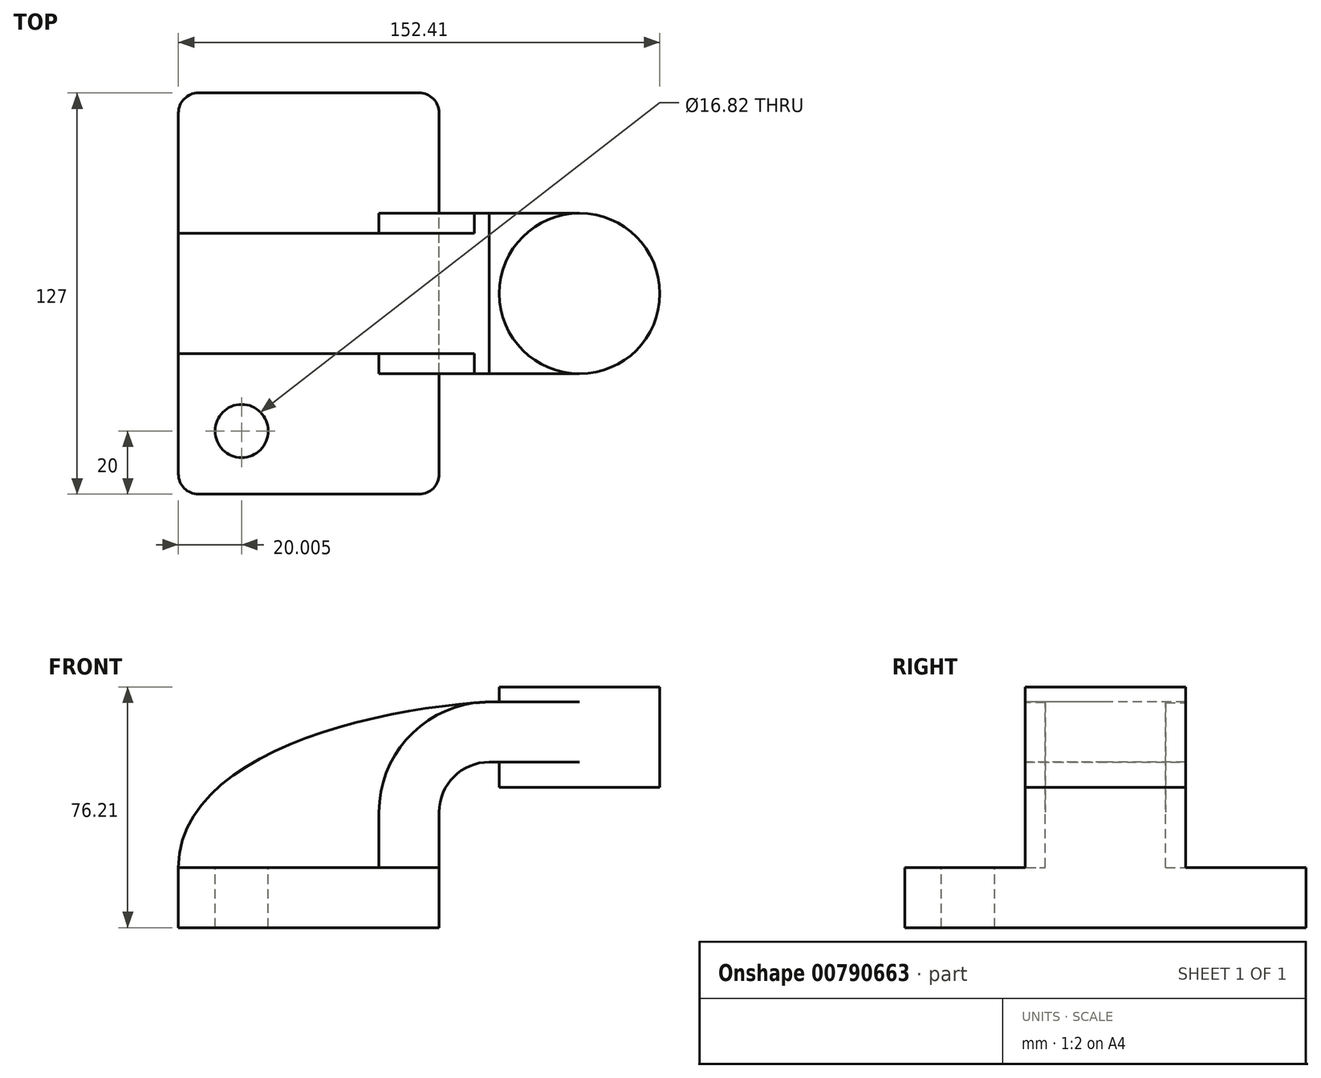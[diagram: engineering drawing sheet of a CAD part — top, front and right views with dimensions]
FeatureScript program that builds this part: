
annotation { "Feature Type Name" : "Feature", "Feature Type Description" : "" }
export const myFeature = defineFeature(function(context is Context, id is Id, definition is map)
    precondition{}
    {
        {
            var Q0;
            Q0=qCreatedBy(makeId("Front.planeOp"),FACE);
            var sketch = newSketch(context, id + "F0", { "sketchPlane" : qUnion([Q0])});
            skLineSegment(sketch, "E0.bottom", {"start": v(41.28, -9.52) * mm, "end": v(-41.28, -9.53) * mm});
            skLineSegment(sketch, "E0.top", {"start": v(41.28, 9.53) * mm, "end": v(-41.28, 9.53) * mm});
            skLineSegment(sketch, "E0.left", {"start": v(41.28, -9.52) * mm, "end": v(41.28, 9.53) * mm});
            skLineSegment(sketch, "E0.right", {"start": v(-41.28, -9.52) * mm, "end": v(-41.28, 9.53) * mm});
            skPoint(sketch, "E0.middle", {"position": v(0, 0) * mm});
            skLineSegment(sketch, "E1.bottom", {"start": v(111.12, 34.93) * mm, "end": v(60.32, 34.93) * mm});
            skLineSegment(sketch, "E1.top", {"start": v(111.12, 66.68) * mm, "end": v(60.32, 66.68) * mm});
            skLineSegment(sketch, "E1.left", {"start": v(111.12, 34.93) * mm, "end": v(111.12, 66.68) * mm});
            skLineSegment(sketch, "E1.right", {"start": v(60.32, 34.93) * mm, "end": v(60.32, 66.68) * mm});
            skPoint(sketch, "E1.middle", {"position": v(85.72, 50.8) * mm});
            skLineSegment(sketch, "E2", {"start": v(41.28, 9.53) * mm, "end": v(41.28, 27) * mm});
            skArc(sketch, "E3", {"start": v(41.27, 27) * mm, "mid": v(45.92, 38.23) * mm, "end": v(57.15, 42.88) * mm});
            skLineSegment(sketch, "E4", {"start": v(57.15, 42.88) * mm, "end": v(85.72, 42.88) * mm});
            skLineSegment(sketch, "E5.0", {"start": v(57.15, 61.93) * mm, "end": v(85.72, 61.93) * mm});
            skArc(sketch, "E5.1", {"start": v(22.23, 27) * mm, "mid": v(32.45, 51.7) * mm, "end": v(57.15, 61.93) * mm});
            skLineSegment(sketch, "E5.2", {"start": v(22.22, 9.53) * mm, "end": v(22.22, 27) * mm});
            skLineSegment(sketch, "E6", {"start": v(85.72, 34.93) * mm, "end": v(85.72, 66.68) * mm});
            skFitSpline(sketch, "E7", {"points": [v(-41.28, 9.52) * mm, v(57.15, 61.93) * mm], "startDerivative": vector(0.89, 108.07) * mm, "endDerivative": vector(112.76, 6.3) * mm});
            skSolve(sketch);
        }
        {
            var Q0;
            Q0=makeQuery(id+"F0.imprint","IMPRINT",FACE,{"disambiguationData":[TD([[makeQuery(id+"F0.imprint","IMPRINT",EDGE,{"derivedFrom":sQuery(id+"F0.wireOp",EDGE,"E0.bottom")}),-1.0]])]});
            extrude(context, id + "F1", {"entities" : qUnion([Q0]), "endBound" : BoundingType.SYMMETRIC, "depth" : 127 * mm, "offsetDistance" : 25.4 * mm});
        }
        {
            var Q0;
            {var subQ1=sQuery(id+"F0.wireOp",EDGE,"E2");Q0=makeQuery(id+"F0.imprint","IMPRINT",FACE,{"disambiguationData":[TD([[makeQuery(id+"F0.imprint","IMPRINT",EDGE,{"derivedFrom":subQ1}),1.0]])]});}
            var Q1;
            {var subQ0=sQuery(id+"F0.wireOp",EDGE,"E4");var subQ1=sQuery(id+"F0.wireOp",EDGE,"E1.right");var subQ2=makeQuery(id+"F0.imprint","INTERSECT",VERTEX,{"derivedFrom":[subQ1,subQ0]});Q1=makeQuery(id+"F0.imprint","IMPRINT",FACE,{"disambiguationData":[TD([[makeQuery(id+"F0.imprint","IMPRINT",EDGE,{"disambiguationData":[TD([[subQ2,-1.0]])],"derivedFrom":subQ1}),-1.0]])]});}
            extrude(context, id + "F2", {"entities" : qUnion([Q0, Q1]), "operationType" : NewBodyOperationType.ADD, "endBound" : BoundingType.SYMMETRIC, "depth" : 50.8 * mm, "offsetDistance" : 25.4 * mm});
        }
        {
            var Q0;
            {var subQ0=sQuery(id+"F0.wireOp",EDGE,"E1.left");Q0=makeQuery(id+"F0.imprint","IMPRINT",FACE,{"disambiguationData":[TD([[makeQuery(id+"F0.imprint","IMPRINT",EDGE,{"derivedFrom":subQ0}),1.0]])]});}
            var Q1;
            Q1=sQuery(id+"F0.wireOp",EDGE,"E6");
            revolve(context, id + "F3", {"operationType" : NewBodyOperationType.ADD, "surfaceOperationType" : NewSurfaceOperationType.NEW, "entities" : qUnion([Q0]), "axis" : qUnion([Q1]), "revolveType" : RevolveType.FULL});
        }
        {
            var Q0;
            {var subQ3=sQuery(id+"F0.wireOp",EDGE,"E5.2");Q0=makeQuery(id+"F0.imprint","IMPRINT",FACE,{"disambiguationData":[TD([[makeQuery(id+"F0.imprint","IMPRINT",EDGE,{"derivedFrom":subQ3}),1.0]])]});}
            extrude(context, id + "F4", {"entities" : qUnion([Q0]), "operationType" : NewBodyOperationType.ADD, "endBound" : BoundingType.SYMMETRIC, "depth" : 38.1 * mm, "offsetDistance" : 25.4 * mm});
        }
        {
            var Q0;
            Q0=makeQuery(id+"F1.opExtrude","CAP_EDGE",EDGE,{"disambiguationData":[OSD([sQuery(id+"F0.wireOp",EDGE,"E0.left")])],"isStart":false});
            var Q1;
            Q1=makeQuery(id+"F1.opExtrude","CAP_EDGE",EDGE,{"disambiguationData":[OSD([sQuery(id+"F0.wireOp",EDGE,"E0.right")])],"isStart":false});
            var Q2;
            Q2=makeQuery(id+"F1.opExtrude","CAP_EDGE",EDGE,{"disambiguationData":[OSD([sQuery(id+"F0.wireOp",EDGE,"E0.left")])],"isStart":true});
            var Q3;
            Q3=makeQuery(id+"F1.opExtrude","CAP_EDGE",EDGE,{"disambiguationData":[OSD([sQuery(id+"F0.wireOp",EDGE,"E0.right")])],"isStart":true});
            fillet(context, id + "F5", {"entities" : qUnion([Q0, Q1, Q2, Q3]), "radius" : 6.35 * mm, "tangentPropagation" : true, "allowEdgeOverflow" : false});
        }
        {
            var Q0;
            {var subQ4=sQuery(id+"F0.wireOp",EDGE,"E0.top");var subQ5=sQuery(id+"F0.wireOp",EDGE,"E0.right");var subQ6=sQuery(id+"F0.wireOp",EDGE,"E0.left");Q0=makeQuery(id+"F4.boolean.opBoolean","SPLIT",FACE,{"disambiguationData":[TD([makeQuery(id+"F1.opExtrude","CAP_FACE",FACE,{"disambiguationData":[OSD([sQuery(id+"F0.wireOp",EDGE,"E0.bottom"),subQ4,subQ6,subQ5])],"isStart":false})])],"derivedFrom":makeQuery(id+"F1.opExtrude","SWEPT_FACE",FACE,{"disambiguationData":[OSD([subQ4])]})});}
            var sketch = newSketch(context, id + "F6", { "sketchPlane" : qUnion([Q0])});
            skCircle(sketch, "E8", {"center": v(-21.28, -43.5) * mm, "radius": 8.41 * mm});
            skSolve(sketch);
        }
        {
            var Q0;
            Q0 = qSketchRegion(id + "F6", true);
            extrude(context, id + "F7", {"entities" : qUnion([Q0]), "operationType" : NewBodyOperationType.REMOVE, "endBound" : BoundingType.THROUGH_ALL, "oppositeDirection" : true, "depth" : 25 * mm, "offsetDistance" : 25 * mm});
        }
    });
